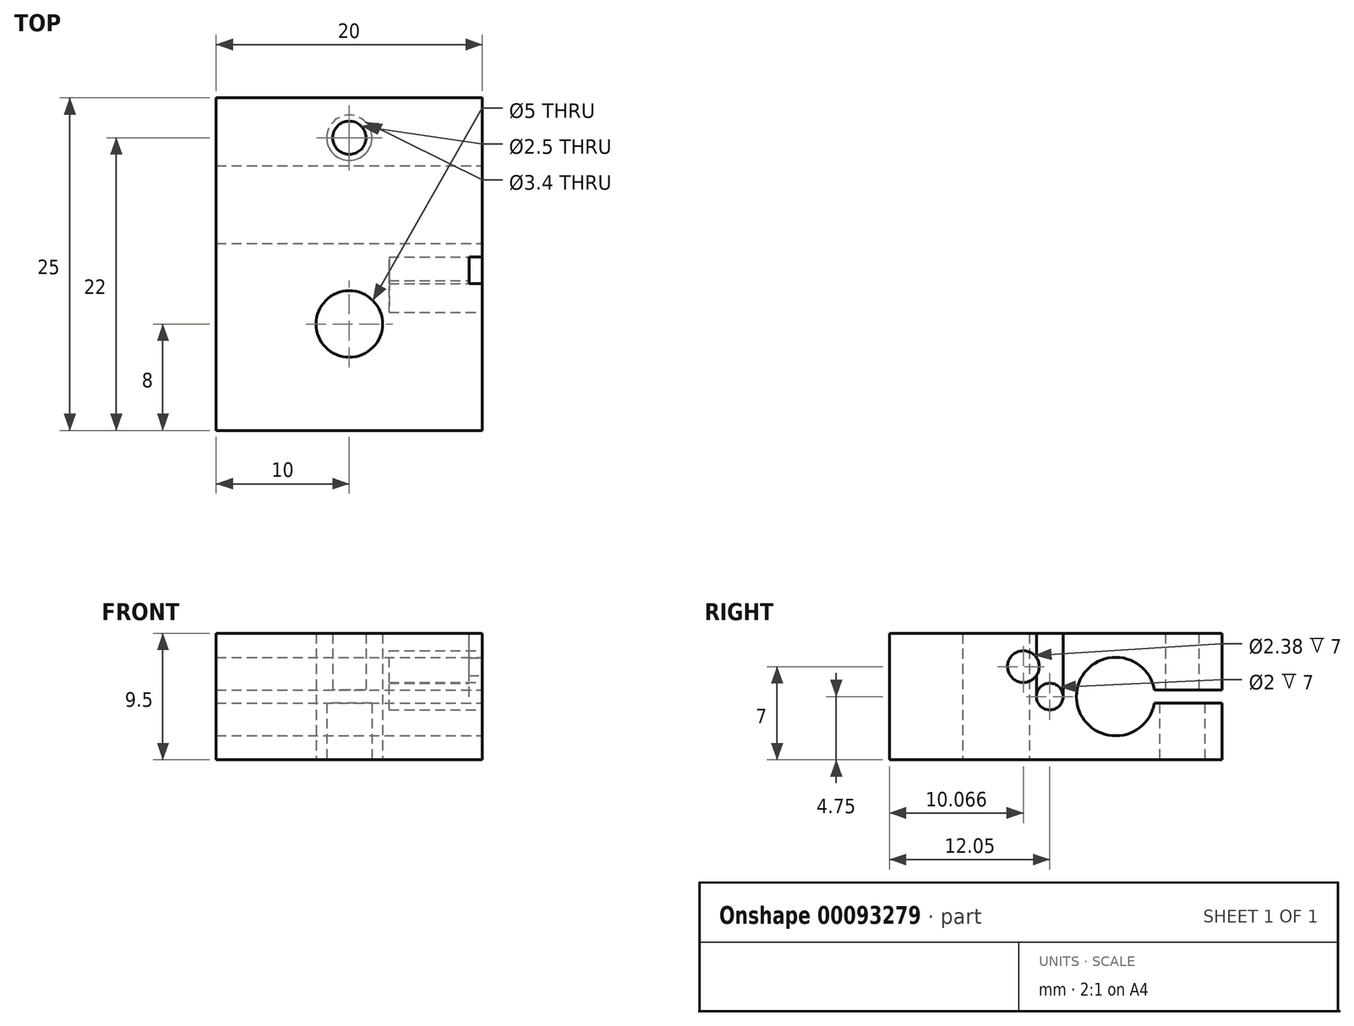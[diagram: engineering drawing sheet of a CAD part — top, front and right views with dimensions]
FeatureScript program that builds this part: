
annotation { "Feature Type Name" : "Feature", "Feature Type Description" : "" }
export const myFeature = defineFeature(function(context is Context, id is Id, definition is map)
    precondition{}
    {
        {
            var Q0;
            Q0=qCreatedBy(makeId("Top.planeOp"),FACE);
            var sketch = newSketch(context, id + "F0", { "sketchPlane" : qUnion([Q0])});
            skLineSegment(sketch, "E0.bottom", {"start": v(10, -12.5) * mm, "end": v(-10, -12.5) * mm});
            skLineSegment(sketch, "E0.top", {"start": v(10, 12.5) * mm, "end": v(-10, 12.5) * mm});
            skLineSegment(sketch, "E0.left", {"start": v(10, -12.5) * mm, "end": v(10, 12.5) * mm});
            skLineSegment(sketch, "E0.right", {"start": v(-10, -12.5) * mm, "end": v(-10, 12.5) * mm});
            skPoint(sketch, "E0.middle", {"position": v(0, 0) * mm});
            skCircle(sketch, "E1", {"center": v(0, -4.5) * mm, "radius": 2.5 * mm});
            skCircle(sketch, "E2", {"center": v(0, 9.5) * mm, "radius": 1.25 * mm});
            skSolve(sketch);
        }
        {
            var Q0;
            Q0 = qSketchRegion(id + "F0", true);
            extrude(context, id + "F1", {"entities" : qUnion([Q0]), "endBound" : BoundingType.SYMMETRIC, "depth" : 9.5 * mm});
        }
        {
            var Q0;
            Q0=makeQuery(id+"F1.opExtrude","SWEPT_FACE",FACE,{"disambiguationData":[OSD([sQuery(id+"F0.wireOp",EDGE,"E0.left")])]});
            var sketch = newSketch(context, id + "F2", { "sketchPlane" : qUnion([Q0])});
            skCircle(sketch, "E3", {"center": v(4.5, 0) * mm, "radius": 2.95 * mm});
            skLineSegment(sketch, "E4.bottom", {"start": v(12.5, -0.5) * mm, "end": v(7.4, -0.5) * mm});
            skLineSegment(sketch, "E4.top", {"start": v(12.5, 0.5) * mm, "end": v(7.4, 0.5) * mm});
            skLineSegment(sketch, "E4.left", {"start": v(12.5, -0.5) * mm, "end": v(12.5, 0.5) * mm});
            skLineSegment(sketch, "E4.right", {"start": v(7.4, -0.5) * mm, "end": v(7.4, 0.5) * mm});
            skPoint(sketch, "E4.middle", {"position": v(9.95, 0) * mm});
            skSolve(sketch);
        }
        {
            var Q0;
            Q0 = qSketchRegion(id + "F2", true);
            extrude(context, id + "F3", {"entities" : qUnion([Q0]), "operationType" : NewBodyOperationType.REMOVE, "endBound" : BoundingType.THROUGH_ALL, "oppositeDirection" : true, "depth" : 25 * mm});
        }
        {
            var Q0;
            Q0=makeQuery(id+"F1.opExtrude","CAP_FACE",FACE,{"disambiguationData":[OSD([sQuery(id+"F0.wireOp",EDGE,"E0.bottom"),sQuery(id+"F0.wireOp",EDGE,"E0.top"),sQuery(id+"F0.wireOp",EDGE,"E0.left"),sQuery(id+"F0.wireOp",EDGE,"E0.right"),sQuery(id+"F0.wireOp",EDGE,"E1"),sQuery(id+"F0.wireOp",EDGE,"E2")])],"isStart":true});
            var sketch = newSketch(context, id + "F4", { "sketchPlane" : qUnion([Q0])});
            skCircle(sketch, "E5", {"center": v(0, -9.5) * mm, "radius": 1.7 * mm});
            skSolve(sketch);
        }
        {
            var Q0;
            Q0 = qSketchRegion(id + "F4", true);
            var Q1;
            Q1=sQuery(id+"F4.wireOp",EDGE,"E5");
            var Q2;
            Q2=makeQuery(id+"F3.boolean.opBoolean","COPY",FACE,{"derivedFrom":makeQuery(id+"F3.opExtrude","SWEPT_FACE",FACE,{"disambiguationData":[OSD([sQuery(id+"F2.wireOp",EDGE,"E4.bottom")])]})});
            extrude(context, id + "F5", {"entities" : qUnion([Q0]), "operationType" : NewBodyOperationType.REMOVE, "surfaceEntities" : qUnion([Q1]), "endBound" : BoundingType.UP_TO_SURFACE, "oppositeDirection" : true, "endBoundEntityFace" : qUnion([Q2]), "depth" : 25 * mm});
        }
        {
            var Q0;
            Q0=makeQuery(id+"F1.opExtrude","SWEPT_FACE",FACE,{"disambiguationData":[OSD([sQuery(id+"F0.wireOp",EDGE,"E0.left")])]});
            var sketch = newSketch(context, id + "F6", { "sketchPlane" : qUnion([Q0])});
            skCircle(sketch, "E6", {"center": v(-0.45, 0) * mm, "radius": 1 * mm});
            skCircle(sketch, "E7", {"center": v(-2.43, 2.25) * mm, "radius": 1.2 * mm});
            skSolve(sketch);
        }
        {
            var Q0;
            Q0 = qSketchRegion(id + "F6", true);
            extrude(context, id + "F7", {"entities" : qUnion([Q0]), "operationType" : NewBodyOperationType.REMOVE, "oppositeDirection" : true, "depth" : 7 * mm});
        }
        {
            var Q0;
            Q0=makeQuery(id+"F1.opExtrude","SWEPT_FACE",FACE,{"disambiguationData":[OSD([sQuery(id+"F0.wireOp",EDGE,"E0.left")])]});
            var sketch = newSketch(context, id + "F8", { "sketchPlane" : qUnion([Q0])});
            skLineSegment(sketch, "E8.bottom", {"start": v(0.55, 0) * mm, "end": v(-1.45, 0) * mm});
            skLineSegment(sketch, "E8.top", {"start": v(0.55, 4.75) * mm, "end": v(-1.45, 4.75) * mm});
            skLineSegment(sketch, "E8.left", {"start": v(0.55, 0) * mm, "end": v(0.55, 4.75) * mm});
            skLineSegment(sketch, "E8.right", {"start": v(-1.45, 0) * mm, "end": v(-1.45, 4.75) * mm});
            skPoint(sketch, "E8.middle", {"position": v(-0.45, 2.38) * mm});
            skLineSegment(sketch, "E9", {"start": v(-0.45, 2.38) * mm, "end": v(-0.45, 0) * mm, "construction": true});
            skSolve(sketch);
        }
        {
            var Q0;
            Q0 = qSketchRegion(id + "F8", true);
            extrude(context, id + "F9", {"entities" : qUnion([Q0]), "operationType" : NewBodyOperationType.REMOVE, "oppositeDirection" : true, "depth" : 1 * mm});
        }
    });
